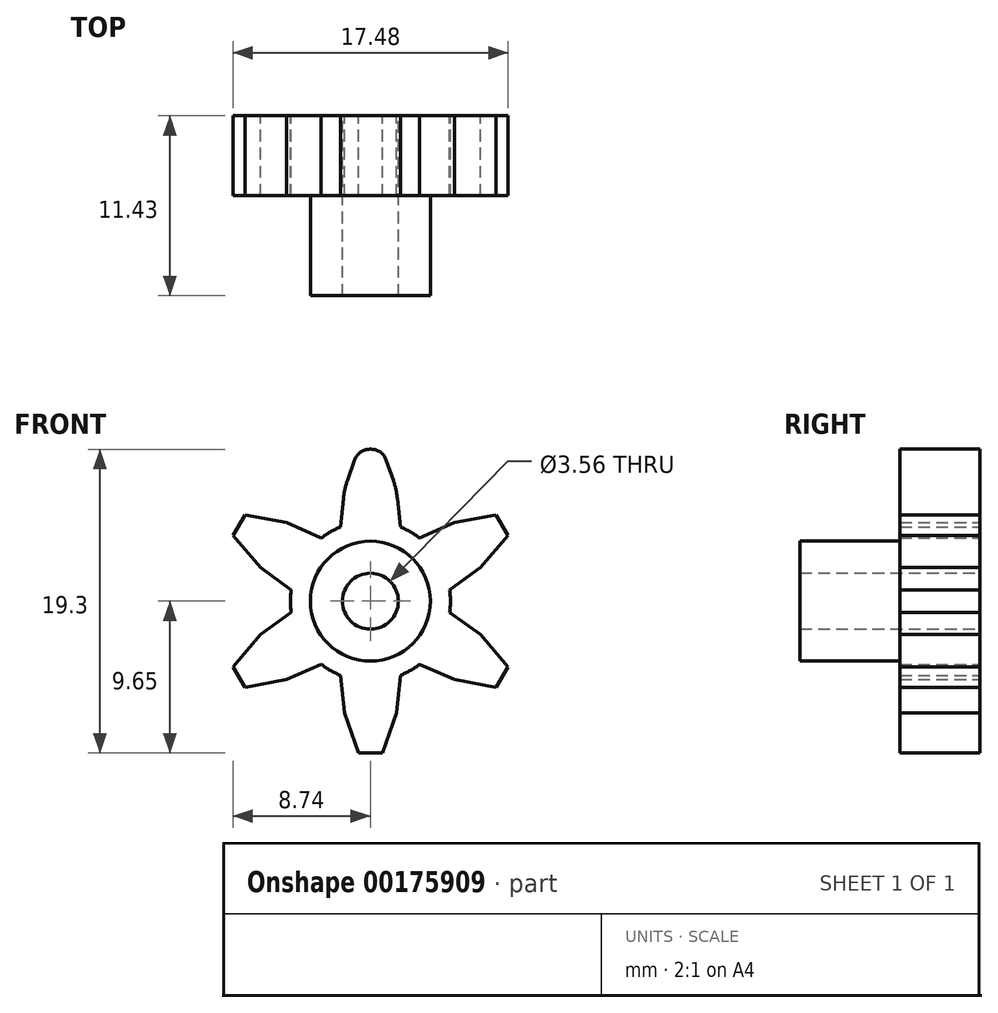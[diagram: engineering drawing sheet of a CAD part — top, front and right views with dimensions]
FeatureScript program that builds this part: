
annotation { "Feature Type Name" : "Feature", "Feature Type Description" : "" }
export const myFeature = defineFeature(function(context is Context, id is Id, definition is map)
    precondition{}
    {
        {
            var Q0;
            Q0=qCreatedBy(makeId("Front.planeOp"),FACE);
            var sketch = newSketch(context, id + "F0", { "sketchPlane" : qUnion([Q0])});
            skCircle(sketch, "E0", {"center": v(0, 0) * mm, "radius": 5.08 * mm});
            skLineSegment(sketch, "E1", {"start": v(-1.9, 4.7) * mm, "end": v(-0.76, 9.65) * mm, "construction": true});
            skLineSegment(sketch, "E2", {"start": v(-0.76, 9.65) * mm, "end": v(0.76, 9.65) * mm});
            skLineSegment(sketch, "E3", {"start": v(0.76, 9.65) * mm, "end": v(1.9, 4.7) * mm, "construction": true});
            skLineSegment(sketch, "E4", {"start": v(-1.9, 4.7) * mm, "end": v(-1.65, 7.11) * mm});
            skPoint(sketch, "E4.endSnap0", {"position": v(-1.33, 7.18) * mm});
            skLineSegment(sketch, "E5", {"start": v(-1.65, 7.11) * mm, "end": v(-0.76, 9.65) * mm});
            skLineSegment(sketch, "E6", {"start": v(1.9, 4.7) * mm, "end": v(1.65, 7.11) * mm});
            skPoint(sketch, "E6.endSnap0", {"position": v(1.33, 7.18) * mm});
            skLineSegment(sketch, "E7", {"start": v(1.65, 7.11) * mm, "end": v(0.76, 9.65) * mm});
            skCircle(sketch, "E8", {"center": v(0, 0) * mm, "radius": 1.78 * mm});
            skLineSegment(sketch, "E9.1.0", {"start": v(-5.03, 0.7) * mm, "end": v(-6.98, 2.13) * mm});
            skLineSegment(sketch, "E9.1.1", {"start": v(-3.13, 4) * mm, "end": v(-5.33, 4.99) * mm});
            skLineSegment(sketch, "E9.1.2", {"start": v(-5.33, 4.99) * mm, "end": v(-7.98, 5.49) * mm});
            skLineSegment(sketch, "E9.1.3", {"start": v(-8.74, 4.17) * mm, "end": v(-7.98, 5.49) * mm});
            skLineSegment(sketch, "E9.1.4", {"start": v(-6.98, 2.13) * mm, "end": v(-8.74, 4.17) * mm});
            skLineSegment(sketch, "E9.2.0", {"start": v(-3.13, -4) * mm, "end": v(-5.33, -4.99) * mm});
            skLineSegment(sketch, "E9.2.1", {"start": v(-5.03, -0.7) * mm, "end": v(-6.98, -2.13) * mm});
            skLineSegment(sketch, "E9.2.2", {"start": v(-6.98, -2.13) * mm, "end": v(-8.74, -4.17) * mm});
            skLineSegment(sketch, "E9.2.3", {"start": v(-7.98, -5.49) * mm, "end": v(-8.74, -4.17) * mm});
            skLineSegment(sketch, "E9.2.4", {"start": v(-5.33, -4.99) * mm, "end": v(-7.98, -5.49) * mm});
            skLineSegment(sketch, "E9.3.0", {"start": v(1.9, -4.7) * mm, "end": v(1.65, -7.11) * mm});
            skLineSegment(sketch, "E9.3.1", {"start": v(-1.9, -4.7) * mm, "end": v(-1.65, -7.11) * mm});
            skLineSegment(sketch, "E9.3.2", {"start": v(-1.65, -7.11) * mm, "end": v(-0.76, -9.65) * mm});
            skLineSegment(sketch, "E9.3.3", {"start": v(0.76, -9.65) * mm, "end": v(-0.76, -9.65) * mm});
            skLineSegment(sketch, "E9.3.4", {"start": v(1.65, -7.11) * mm, "end": v(0.76, -9.65) * mm});
            skLineSegment(sketch, "E9.4.0", {"start": v(5.03, -0.7) * mm, "end": v(6.98, -2.13) * mm});
            skLineSegment(sketch, "E9.4.1", {"start": v(3.13, -4) * mm, "end": v(5.33, -4.99) * mm});
            skLineSegment(sketch, "E9.4.2", {"start": v(5.33, -4.99) * mm, "end": v(7.98, -5.49) * mm});
            skLineSegment(sketch, "E9.4.3", {"start": v(8.74, -4.17) * mm, "end": v(7.98, -5.49) * mm});
            skLineSegment(sketch, "E9.4.4", {"start": v(6.98, -2.13) * mm, "end": v(8.74, -4.17) * mm});
            skLineSegment(sketch, "E9.5.0", {"start": v(3.13, 4) * mm, "end": v(5.33, 4.99) * mm});
            skLineSegment(sketch, "E9.5.1", {"start": v(5.03, 0.7) * mm, "end": v(6.98, 2.13) * mm});
            skLineSegment(sketch, "E9.5.2", {"start": v(6.98, 2.13) * mm, "end": v(8.74, 4.17) * mm});
            skLineSegment(sketch, "E9.5.3", {"start": v(7.98, 5.49) * mm, "end": v(8.74, 4.17) * mm});
            skLineSegment(sketch, "E9.5.4", {"start": v(5.33, 4.99) * mm, "end": v(7.98, 5.49) * mm});
            skSolve(sketch);
        }
        {
            var Q0;
            Q0=qSketchRegion(id+"F0",true);
            extrude(context, id + "F1", {"entities" : qUnion([Q0]), "depth" : 5.08 * mm});
        }
        {
            var Q0;
            Q0=makeQuery(id+"F1.opExtrude","CAP_FACE",FACE,{"disambiguationData":[OSD([sQuery(id+"F0.wireOp",EDGE,"E0"),sQuery(id+"F0.wireOp",EDGE,"E2"),sQuery(id+"F0.wireOp",EDGE,"E4"),sQuery(id+"F0.wireOp",EDGE,"E5"),sQuery(id+"F0.wireOp",EDGE,"E6"),sQuery(id+"F0.wireOp",EDGE,"E7"),sQuery(id+"F0.wireOp",EDGE,"9ba0eadd-e692-48d7-a6a5-f7137d904180.1.0"),sQuery(id+"F0.wireOp",EDGE,"9ba0eadd-e692-48d7-a6a5-f7137d904180.1.1"),sQuery(id+"F0.wireOp",EDGE,"9ba0eadd-e692-48d7-a6a5-f7137d904180.1.2"),sQuery(id+"F0.wireOp",EDGE,"9ba0eadd-e692-48d7-a6a5-f7137d904180.1.3"),sQuery(id+"F0.wireOp",EDGE,"9ba0eadd-e692-48d7-a6a5-f7137d904180.1.4"),sQuery(id+"F0.wireOp",EDGE,"9ba0eadd-e692-48d7-a6a5-f7137d904180.2.0"),sQuery(id+"F0.wireOp",EDGE,"9ba0eadd-e692-48d7-a6a5-f7137d904180.2.1"),sQuery(id+"F0.wireOp",EDGE,"9ba0eadd-e692-48d7-a6a5-f7137d904180.2.2"),sQuery(id+"F0.wireOp",EDGE,"9ba0eadd-e692-48d7-a6a5-f7137d904180.2.3"),sQuery(id+"F0.wireOp",EDGE,"9ba0eadd-e692-48d7-a6a5-f7137d904180.2.4"),sQuery(id+"F0.wireOp",EDGE,"9ba0eadd-e692-48d7-a6a5-f7137d904180.3.0"),sQuery(id+"F0.wireOp",EDGE,"9ba0eadd-e692-48d7-a6a5-f7137d904180.3.1"),sQuery(id+"F0.wireOp",EDGE,"9ba0eadd-e692-48d7-a6a5-f7137d904180.3.2"),sQuery(id+"F0.wireOp",EDGE,"9ba0eadd-e692-48d7-a6a5-f7137d904180.3.3"),sQuery(id+"F0.wireOp",EDGE,"9ba0eadd-e692-48d7-a6a5-f7137d904180.3.4"),sQuery(id+"F0.wireOp",EDGE,"9ba0eadd-e692-48d7-a6a5-f7137d904180.4.0"),sQuery(id+"F0.wireOp",EDGE,"9ba0eadd-e692-48d7-a6a5-f7137d904180.4.1"),sQuery(id+"F0.wireOp",EDGE,"9ba0eadd-e692-48d7-a6a5-f7137d904180.4.2"),sQuery(id+"F0.wireOp",EDGE,"9ba0eadd-e692-48d7-a6a5-f7137d904180.4.3"),sQuery(id+"F0.wireOp",EDGE,"9ba0eadd-e692-48d7-a6a5-f7137d904180.4.4"),sQuery(id+"F0.wireOp",EDGE,"9ba0eadd-e692-48d7-a6a5-f7137d904180.5.0"),sQuery(id+"F0.wireOp",EDGE,"9ba0eadd-e692-48d7-a6a5-f7137d904180.5.1"),sQuery(id+"F0.wireOp",EDGE,"9ba0eadd-e692-48d7-a6a5-f7137d904180.5.2"),sQuery(id+"F0.wireOp",EDGE,"9ba0eadd-e692-48d7-a6a5-f7137d904180.5.3"),sQuery(id+"F0.wireOp",EDGE,"9ba0eadd-e692-48d7-a6a5-f7137d904180.5.4"),sQuery(id+"F0.wireOp",EDGE,"9ba0eadd-e692-48d7-a6a5-f7137d904180.6.0"),sQuery(id+"F0.wireOp",EDGE,"9ba0eadd-e692-48d7-a6a5-f7137d904180.6.1"),sQuery(id+"F0.wireOp",EDGE,"9ba0eadd-e692-48d7-a6a5-f7137d904180.6.2"),sQuery(id+"F0.wireOp",EDGE,"9ba0eadd-e692-48d7-a6a5-f7137d904180.6.3"),sQuery(id+"F0.wireOp",EDGE,"9ba0eadd-e692-48d7-a6a5-f7137d904180.6.4"),sQuery(id+"F0.wireOp",EDGE,"9ba0eadd-e692-48d7-a6a5-f7137d904180.7.0"),sQuery(id+"F0.wireOp",EDGE,"9ba0eadd-e692-48d7-a6a5-f7137d904180.7.1"),sQuery(id+"F0.wireOp",EDGE,"9ba0eadd-e692-48d7-a6a5-f7137d904180.7.2"),sQuery(id+"F0.wireOp",EDGE,"9ba0eadd-e692-48d7-a6a5-f7137d904180.7.3"),sQuery(id+"F0.wireOp",EDGE,"9ba0eadd-e692-48d7-a6a5-f7137d904180.7.4"),sQuery(id+"F0.wireOp",EDGE,"9ba0eadd-e692-48d7-a6a5-f7137d904180.8.0"),sQuery(id+"F0.wireOp",EDGE,"9ba0eadd-e692-48d7-a6a5-f7137d904180.8.1"),sQuery(id+"F0.wireOp",EDGE,"9ba0eadd-e692-48d7-a6a5-f7137d904180.8.2"),sQuery(id+"F0.wireOp",EDGE,"9ba0eadd-e692-48d7-a6a5-f7137d904180.8.3"),sQuery(id+"F0.wireOp",EDGE,"9ba0eadd-e692-48d7-a6a5-f7137d904180.8.4"),sQuery(id+"F0.wireOp",EDGE,"9ba0eadd-e692-48d7-a6a5-f7137d904180.9.0"),sQuery(id+"F0.wireOp",EDGE,"9ba0eadd-e692-48d7-a6a5-f7137d904180.9.1"),sQuery(id+"F0.wireOp",EDGE,"9ba0eadd-e692-48d7-a6a5-f7137d904180.9.2"),sQuery(id+"F0.wireOp",EDGE,"9ba0eadd-e692-48d7-a6a5-f7137d904180.9.3"),sQuery(id+"F0.wireOp",EDGE,"9ba0eadd-e692-48d7-a6a5-f7137d904180.9.4"),sQuery(id+"F0.wireOp",EDGE,"E8")])],"isStart":false});
            var sketch = newSketch(context, id + "F2", { "sketchPlane" : qUnion([Q0])});
            skCircle(sketch, "E10.0", {"center": v(0, 0) * mm, "radius": 1.78 * mm});
            skCircle(sketch, "E11", {"center": v(0, 0) * mm, "radius": 3.81 * mm});
            skSolve(sketch);
        }
        {
            var Q0;
            Q0=qSketchRegion(id+"F2",true);
            extrude(context, id + "F3", {"entities" : qUnion([Q0]), "operationType" : NewBodyOperationType.ADD, "depth" : 6.35 * mm});
        }
        {
            var Q0;
            Q0=makeQuery(id+"F1.opExtrude","SWEPT_EDGE",EDGE,{"disambiguationData":[OSD([sQuery(id+"F0.wireOp",EDGE,"9ba0eadd-e692-48d7-a6a5-f7137d904180.9.1"),sQuery(id+"F0.wireOp",EDGE,"9ba0eadd-e692-48d7-a6a5-f7137d904180.9.2")])]});
            var Q1;
            Q1=makeQuery(id+"F1.opExtrude","SWEPT_EDGE",EDGE,{"disambiguationData":[OSD([sQuery(id+"F0.wireOp",EDGE,"9ba0eadd-e692-48d7-a6a5-f7137d904180.9.3"),sQuery(id+"F0.wireOp",EDGE,"9ba0eadd-e692-48d7-a6a5-f7137d904180.9.4")])]});
            var Q2;
            Q2=makeQuery(id+"F1.opExtrude","SWEPT_EDGE",EDGE,{"disambiguationData":[OSD([sQuery(id+"F0.wireOp",EDGE,"E6"),sQuery(id+"F0.wireOp",EDGE,"E7")])]});
            var Q3;
            Q3=makeQuery(id+"F1.opExtrude","SWEPT_EDGE",EDGE,{"disambiguationData":[OSD([sQuery(id+"F0.wireOp",EDGE,"9ba0eadd-e692-48d7-a6a5-f7137d904180.1.1"),sQuery(id+"F0.wireOp",EDGE,"9ba0eadd-e692-48d7-a6a5-f7137d904180.1.2")])]});
            var Q4;
            Q4=makeQuery(id+"F1.opExtrude","SWEPT_EDGE",EDGE,{"disambiguationData":[OSD([sQuery(id+"F0.wireOp",EDGE,"9ba0eadd-e692-48d7-a6a5-f7137d904180.2.1"),sQuery(id+"F0.wireOp",EDGE,"9ba0eadd-e692-48d7-a6a5-f7137d904180.2.2")])]});
            var Q5;
            Q5=makeQuery(id+"F1.opExtrude","SWEPT_EDGE",EDGE,{"disambiguationData":[OSD([sQuery(id+"F0.wireOp",EDGE,"9ba0eadd-e692-48d7-a6a5-f7137d904180.3.1"),sQuery(id+"F0.wireOp",EDGE,"9ba0eadd-e692-48d7-a6a5-f7137d904180.3.2")])]});
            var Q6;
            Q6=makeQuery(id+"F1.opExtrude","SWEPT_EDGE",EDGE,{"disambiguationData":[OSD([sQuery(id+"F0.wireOp",EDGE,"9ba0eadd-e692-48d7-a6a5-f7137d904180.4.1"),sQuery(id+"F0.wireOp",EDGE,"9ba0eadd-e692-48d7-a6a5-f7137d904180.4.2")])]});
            var Q7;
            Q7=makeQuery(id+"F1.opExtrude","SWEPT_EDGE",EDGE,{"disambiguationData":[OSD([sQuery(id+"F0.wireOp",EDGE,"9ba0eadd-e692-48d7-a6a5-f7137d904180.5.1"),sQuery(id+"F0.wireOp",EDGE,"9ba0eadd-e692-48d7-a6a5-f7137d904180.5.2")])]});
            var Q8;
            Q8=makeQuery(id+"F1.opExtrude","SWEPT_EDGE",EDGE,{"disambiguationData":[OSD([sQuery(id+"F0.wireOp",EDGE,"9ba0eadd-e692-48d7-a6a5-f7137d904180.6.1"),sQuery(id+"F0.wireOp",EDGE,"9ba0eadd-e692-48d7-a6a5-f7137d904180.6.2")])]});
            var Q9;
            Q9=makeQuery(id+"F1.opExtrude","SWEPT_EDGE",EDGE,{"disambiguationData":[OSD([sQuery(id+"F0.wireOp",EDGE,"9ba0eadd-e692-48d7-a6a5-f7137d904180.7.1"),sQuery(id+"F0.wireOp",EDGE,"9ba0eadd-e692-48d7-a6a5-f7137d904180.7.2")])]});
            var Q10;
            Q10=makeQuery(id+"F1.opExtrude","SWEPT_EDGE",EDGE,{"disambiguationData":[OSD([sQuery(id+"F0.wireOp",EDGE,"9ba0eadd-e692-48d7-a6a5-f7137d904180.8.1"),sQuery(id+"F0.wireOp",EDGE,"9ba0eadd-e692-48d7-a6a5-f7137d904180.8.2")])]});
            var Q11;
            Q11=makeQuery(id+"F1.opExtrude","SWEPT_EDGE",EDGE,{"disambiguationData":[OSD([sQuery(id+"F0.wireOp",EDGE,"9ba0eadd-e692-48d7-a6a5-f7137d904180.7.3"),sQuery(id+"F0.wireOp",EDGE,"9ba0eadd-e692-48d7-a6a5-f7137d904180.7.4")])]});
            var Q12;
            Q12=makeQuery(id+"F1.opExtrude","SWEPT_EDGE",EDGE,{"disambiguationData":[OSD([sQuery(id+"F0.wireOp",EDGE,"9ba0eadd-e692-48d7-a6a5-f7137d904180.8.3"),sQuery(id+"F0.wireOp",EDGE,"9ba0eadd-e692-48d7-a6a5-f7137d904180.8.4")])]});
            var Q13;
            Q13=makeQuery(id+"F1.opExtrude","SWEPT_EDGE",EDGE,{"disambiguationData":[OSD([sQuery(id+"F0.wireOp",EDGE,"E4"),sQuery(id+"F0.wireOp",EDGE,"E5")])]});
            var Q14;
            Q14=makeQuery(id+"F1.opExtrude","SWEPT_EDGE",EDGE,{"disambiguationData":[OSD([sQuery(id+"F0.wireOp",EDGE,"9ba0eadd-e692-48d7-a6a5-f7137d904180.1.3"),sQuery(id+"F0.wireOp",EDGE,"9ba0eadd-e692-48d7-a6a5-f7137d904180.1.4")])]});
            var Q15;
            Q15=makeQuery(id+"F1.opExtrude","SWEPT_EDGE",EDGE,{"disambiguationData":[OSD([sQuery(id+"F0.wireOp",EDGE,"9ba0eadd-e692-48d7-a6a5-f7137d904180.2.3"),sQuery(id+"F0.wireOp",EDGE,"9ba0eadd-e692-48d7-a6a5-f7137d904180.2.4")])]});
            var Q16;
            Q16=makeQuery(id+"F1.opExtrude","SWEPT_EDGE",EDGE,{"disambiguationData":[OSD([sQuery(id+"F0.wireOp",EDGE,"9ba0eadd-e692-48d7-a6a5-f7137d904180.3.3"),sQuery(id+"F0.wireOp",EDGE,"9ba0eadd-e692-48d7-a6a5-f7137d904180.3.4")])]});
            var Q17;
            Q17=makeQuery(id+"F1.opExtrude","SWEPT_EDGE",EDGE,{"disambiguationData":[OSD([sQuery(id+"F0.wireOp",EDGE,"9ba0eadd-e692-48d7-a6a5-f7137d904180.4.3"),sQuery(id+"F0.wireOp",EDGE,"9ba0eadd-e692-48d7-a6a5-f7137d904180.4.4")])]});
            var Q18;
            Q18=makeQuery(id+"F1.opExtrude","SWEPT_EDGE",EDGE,{"disambiguationData":[OSD([sQuery(id+"F0.wireOp",EDGE,"9ba0eadd-e692-48d7-a6a5-f7137d904180.5.3"),sQuery(id+"F0.wireOp",EDGE,"9ba0eadd-e692-48d7-a6a5-f7137d904180.5.4")])]});
            var Q19;
            Q19=makeQuery(id+"F1.opExtrude","SWEPT_EDGE",EDGE,{"disambiguationData":[OSD([sQuery(id+"F0.wireOp",EDGE,"9ba0eadd-e692-48d7-a6a5-f7137d904180.6.3"),sQuery(id+"F0.wireOp",EDGE,"9ba0eadd-e692-48d7-a6a5-f7137d904180.6.4")])]});
            fillet(context, id + "F4", {"entities" : qUnion([Q0, Q1, Q2, Q3, Q4, Q5, Q6, Q7, Q8, Q9, Q10, Q11, Q12, Q13, Q14, Q15, Q16, Q17, Q18, Q19]), "radius" : 5.08 * mm, "tangentPropagation" : true, "allowEdgeOverflow" : false});
        }
        {
            var Q0;
            Q0=makeQuery(id+"F1.opExtrude","SWEPT_EDGE",EDGE,{"disambiguationData":[OSD([sQuery(id+"F0.wireOp",EDGE,"E2"),sQuery(id+"F0.wireOp",EDGE,"E7")])]});
            var Q1;
            Q1=makeQuery(id+"F1.opExtrude","SWEPT_EDGE",EDGE,{"disambiguationData":[OSD([sQuery(id+"F0.wireOp",EDGE,"E2"),sQuery(id+"F0.wireOp",EDGE,"E5")])]});
            var Q2;
            Q2=makeQuery(id+"F1.opExtrude","SWEPT_EDGE",EDGE,{"disambiguationData":[OSD([sQuery(id+"F0.wireOp",EDGE,"9ba0eadd-e692-48d7-a6a5-f7137d904180.1.0"),sQuery(id+"F0.wireOp",EDGE,"9ba0eadd-e692-48d7-a6a5-f7137d904180.1.1")])]});
            var Q3;
            Q3=makeQuery(id+"F1.opExtrude","SWEPT_EDGE",EDGE,{"disambiguationData":[OSD([sQuery(id+"F0.wireOp",EDGE,"9ba0eadd-e692-48d7-a6a5-f7137d904180.1.0"),sQuery(id+"F0.wireOp",EDGE,"9ba0eadd-e692-48d7-a6a5-f7137d904180.1.3")])]});
            var Q4;
            Q4=makeQuery(id+"F1.opExtrude","SWEPT_EDGE",EDGE,{"disambiguationData":[OSD([sQuery(id+"F0.wireOp",EDGE,"9ba0eadd-e692-48d7-a6a5-f7137d904180.2.0"),sQuery(id+"F0.wireOp",EDGE,"9ba0eadd-e692-48d7-a6a5-f7137d904180.2.1")])]});
            var Q5;
            Q5=makeQuery(id+"F1.opExtrude","SWEPT_EDGE",EDGE,{"disambiguationData":[OSD([sQuery(id+"F0.wireOp",EDGE,"9ba0eadd-e692-48d7-a6a5-f7137d904180.9.0"),sQuery(id+"F0.wireOp",EDGE,"9ba0eadd-e692-48d7-a6a5-f7137d904180.9.3")])]});
            var Q6;
            Q6=makeQuery(id+"F1.opExtrude","SWEPT_EDGE",EDGE,{"disambiguationData":[OSD([sQuery(id+"F0.wireOp",EDGE,"9ba0eadd-e692-48d7-a6a5-f7137d904180.9.0"),sQuery(id+"F0.wireOp",EDGE,"9ba0eadd-e692-48d7-a6a5-f7137d904180.9.1")])]});
            var Q7;
            Q7=makeQuery(id+"F1.opExtrude","SWEPT_EDGE",EDGE,{"disambiguationData":[OSD([sQuery(id+"F0.wireOp",EDGE,"9ba0eadd-e692-48d7-a6a5-f7137d904180.8.0"),sQuery(id+"F0.wireOp",EDGE,"9ba0eadd-e692-48d7-a6a5-f7137d904180.8.3")])]});
            var Q8;
            Q8=makeQuery(id+"F1.opExtrude","SWEPT_EDGE",EDGE,{"disambiguationData":[OSD([sQuery(id+"F0.wireOp",EDGE,"9ba0eadd-e692-48d7-a6a5-f7137d904180.2.0"),sQuery(id+"F0.wireOp",EDGE,"9ba0eadd-e692-48d7-a6a5-f7137d904180.2.3")])]});
            var Q9;
            Q9=makeQuery(id+"F1.opExtrude","SWEPT_EDGE",EDGE,{"disambiguationData":[OSD([sQuery(id+"F0.wireOp",EDGE,"9ba0eadd-e692-48d7-a6a5-f7137d904180.3.0"),sQuery(id+"F0.wireOp",EDGE,"9ba0eadd-e692-48d7-a6a5-f7137d904180.3.1")])]});
            var Q10;
            Q10=makeQuery(id+"F1.opExtrude","SWEPT_EDGE",EDGE,{"disambiguationData":[OSD([sQuery(id+"F0.wireOp",EDGE,"9ba0eadd-e692-48d7-a6a5-f7137d904180.3.0"),sQuery(id+"F0.wireOp",EDGE,"9ba0eadd-e692-48d7-a6a5-f7137d904180.3.3")])]});
            var Q11;
            Q11=makeQuery(id+"F1.opExtrude","SWEPT_EDGE",EDGE,{"disambiguationData":[OSD([sQuery(id+"F0.wireOp",EDGE,"9ba0eadd-e692-48d7-a6a5-f7137d904180.4.0"),sQuery(id+"F0.wireOp",EDGE,"9ba0eadd-e692-48d7-a6a5-f7137d904180.4.1")])]});
            var Q12;
            Q12=makeQuery(id+"F1.opExtrude","SWEPT_EDGE",EDGE,{"disambiguationData":[OSD([sQuery(id+"F0.wireOp",EDGE,"9ba0eadd-e692-48d7-a6a5-f7137d904180.4.0"),sQuery(id+"F0.wireOp",EDGE,"9ba0eadd-e692-48d7-a6a5-f7137d904180.4.3")])]});
            var Q13;
            Q13=makeQuery(id+"F1.opExtrude","SWEPT_EDGE",EDGE,{"disambiguationData":[OSD([sQuery(id+"F0.wireOp",EDGE,"9ba0eadd-e692-48d7-a6a5-f7137d904180.5.0"),sQuery(id+"F0.wireOp",EDGE,"9ba0eadd-e692-48d7-a6a5-f7137d904180.5.1")])]});
            var Q14;
            Q14=makeQuery(id+"F1.opExtrude","SWEPT_EDGE",EDGE,{"disambiguationData":[OSD([sQuery(id+"F0.wireOp",EDGE,"9ba0eadd-e692-48d7-a6a5-f7137d904180.5.0"),sQuery(id+"F0.wireOp",EDGE,"9ba0eadd-e692-48d7-a6a5-f7137d904180.5.3")])]});
            var Q15;
            Q15=makeQuery(id+"F1.opExtrude","SWEPT_EDGE",EDGE,{"disambiguationData":[OSD([sQuery(id+"F0.wireOp",EDGE,"9ba0eadd-e692-48d7-a6a5-f7137d904180.6.0"),sQuery(id+"F0.wireOp",EDGE,"9ba0eadd-e692-48d7-a6a5-f7137d904180.6.1")])]});
            var Q16;
            Q16=makeQuery(id+"F1.opExtrude","SWEPT_EDGE",EDGE,{"disambiguationData":[OSD([sQuery(id+"F0.wireOp",EDGE,"9ba0eadd-e692-48d7-a6a5-f7137d904180.6.0"),sQuery(id+"F0.wireOp",EDGE,"9ba0eadd-e692-48d7-a6a5-f7137d904180.6.3")])]});
            var Q17;
            Q17=makeQuery(id+"F1.opExtrude","SWEPT_EDGE",EDGE,{"disambiguationData":[OSD([sQuery(id+"F0.wireOp",EDGE,"9ba0eadd-e692-48d7-a6a5-f7137d904180.7.0"),sQuery(id+"F0.wireOp",EDGE,"9ba0eadd-e692-48d7-a6a5-f7137d904180.7.3")])]});
            var Q18;
            Q18=makeQuery(id+"F1.opExtrude","SWEPT_EDGE",EDGE,{"disambiguationData":[OSD([sQuery(id+"F0.wireOp",EDGE,"9ba0eadd-e692-48d7-a6a5-f7137d904180.7.0"),sQuery(id+"F0.wireOp",EDGE,"9ba0eadd-e692-48d7-a6a5-f7137d904180.7.1")])]});
            var Q19;
            Q19=makeQuery(id+"F1.opExtrude","SWEPT_EDGE",EDGE,{"disambiguationData":[OSD([sQuery(id+"F0.wireOp",EDGE,"9ba0eadd-e692-48d7-a6a5-f7137d904180.8.0"),sQuery(id+"F0.wireOp",EDGE,"9ba0eadd-e692-48d7-a6a5-f7137d904180.8.1")])]});
            fillet(context, id + "F5", {"entities" : qUnion([Q0, Q1, Q2, Q3, Q4, Q5, Q6, Q7, Q8, Q9, Q10, Q11, Q12, Q13, Q14, Q15, Q16, Q17, Q18, Q19]), "radius" : 1.02 * mm, "tangentPropagation" : true, "allowEdgeOverflow" : false});
        }
    });
